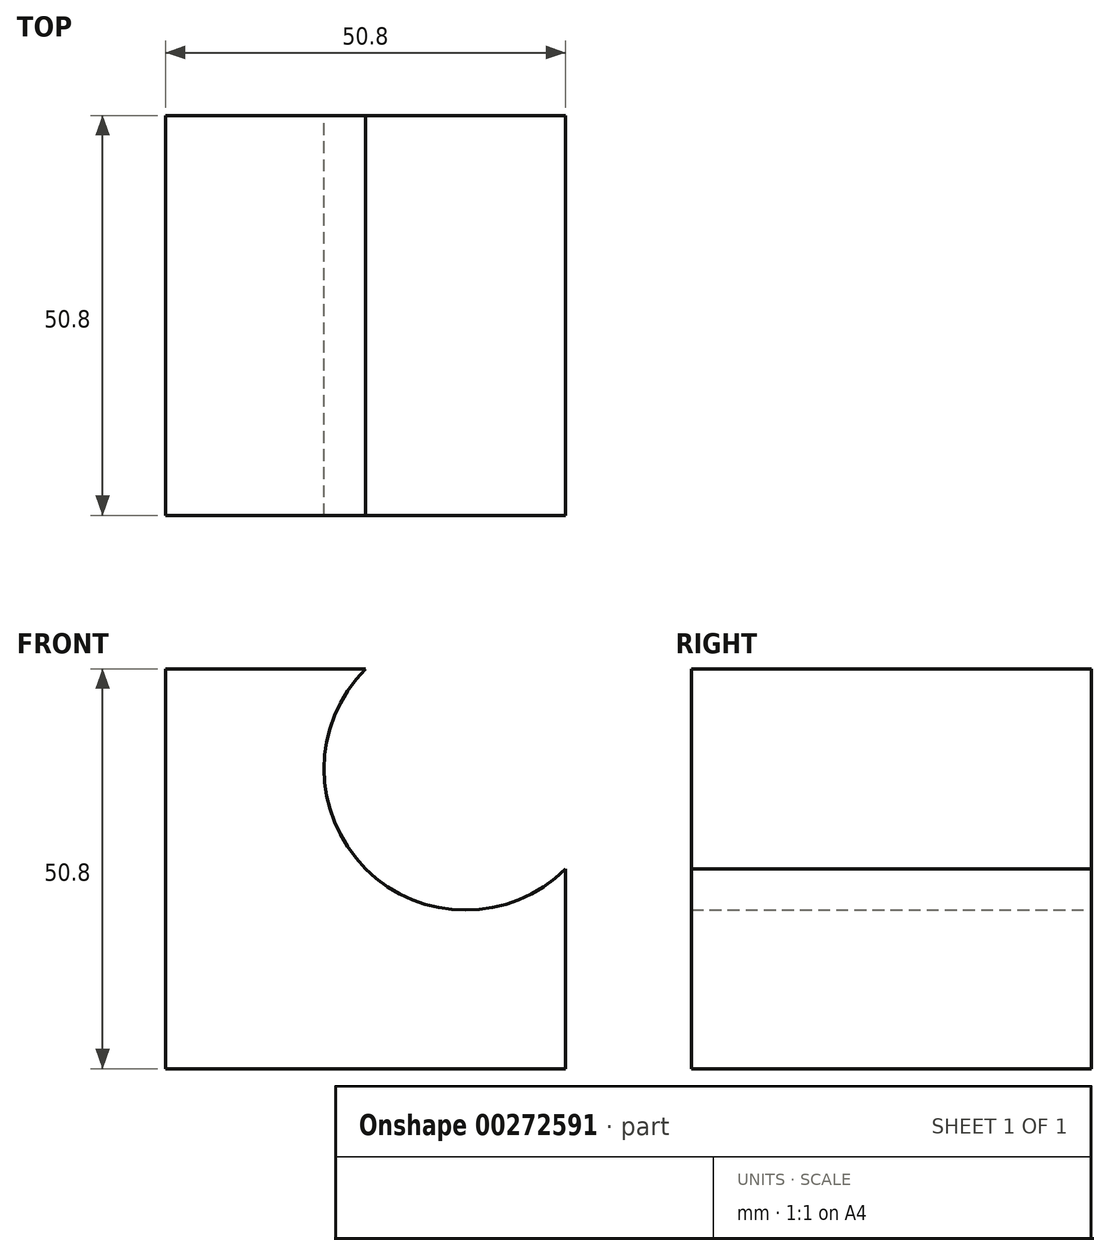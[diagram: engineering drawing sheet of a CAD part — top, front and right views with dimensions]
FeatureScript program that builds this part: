
annotation { "Feature Type Name" : "Feature", "Feature Type Description" : "" }
export const myFeature = defineFeature(function(context is Context, id is Id, definition is map)
    precondition{}
    {
        {
            var Q0;
            Q0=qCreatedBy(makeId("Front.planeOp"),FACE);
            var sketch = newSketch(context, id + "F0", { "sketchPlane" : qUnion([Q0])});
            skLineSegment(sketch, "E0", {"start": v(0, 0) * mm, "end": v(-50.8, 0) * mm});
            skLineSegment(sketch, "E1", {"start": v(-50.8, 0) * mm, "end": v(-50.8, 50.8) * mm});
            skLineSegment(sketch, "E2", {"start": v(-50.8, 50.8) * mm, "end": v(-25.4, 50.8) * mm});
            skLineSegment(sketch, "E3", {"start": v(0, 25.4) * mm, "end": v(0, 0) * mm});
            skArc(sketch, "E4", {"start": v(-25.4, 50.8) * mm, "mid": v(-25.4, 25.4) * mm, "end": v(0, 25.4) * mm});
            skSolve(sketch);
        }
        {
            var Q0;
            Q0 = qSketchRegion(id + "F0", true);
            extrude(context, id + "F1", {"entities" : qUnion([Q0]), "depth" : 50.8 * mm});
        }
    });
